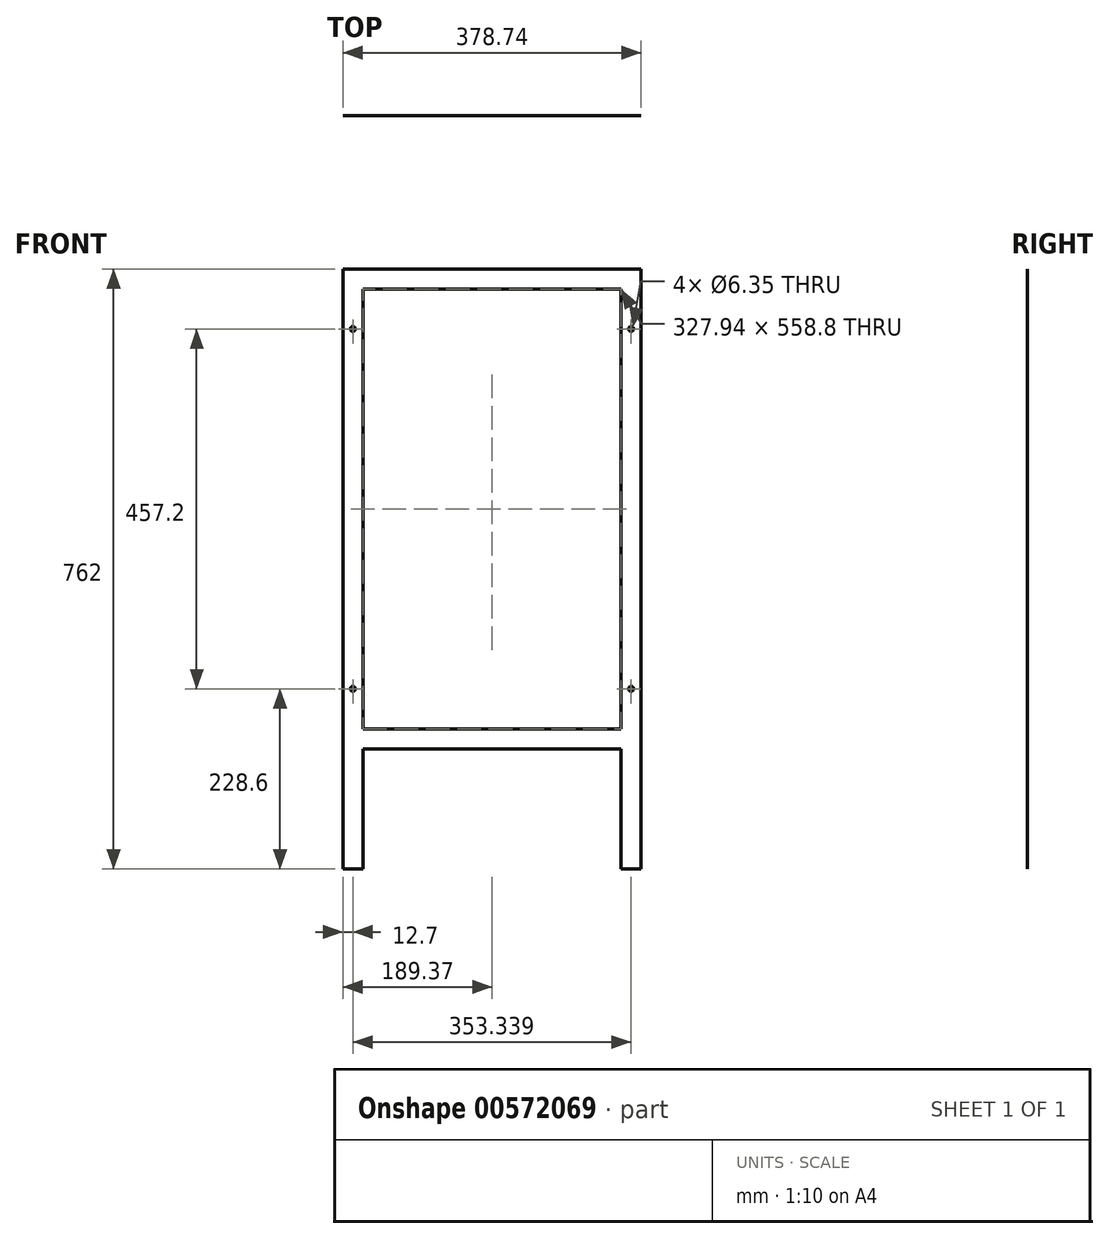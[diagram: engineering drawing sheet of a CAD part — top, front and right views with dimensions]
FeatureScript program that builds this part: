
annotation { "Feature Type Name" : "Feature", "Feature Type Description" : "" }
export const myFeature = defineFeature(function(context is Context, id is Id, definition is map)
    precondition{}
    {
        {
            var Q0;
            Q0=qCreatedBy(makeId("Front.planeOp"),FACE);
            var sketch = newSketch(context, id + "F0", { "sketchPlane" : qUnion([Q0])});
            skLineSegment(sketch, "E0.bottom", {"start": v(189.37, -381) * mm, "end": v(-189.37, -381) * mm});
            skLineSegment(sketch, "E0.top", {"start": v(189.37, 381) * mm, "end": v(-189.37, 381) * mm});
            skLineSegment(sketch, "E0.left", {"start": v(189.37, -381) * mm, "end": v(189.37, 381) * mm});
            skLineSegment(sketch, "E0.right", {"start": v(-189.37, -381) * mm, "end": v(-189.37, 381) * mm});
            skPoint(sketch, "E0.middle", {"position": v(0, 0) * mm});
            skLineSegment(sketch, "E1.bottom", {"start": v(-189.37, 381) * mm, "end": v(189.37, 381) * mm});
            skLineSegment(sketch, "E1.top", {"start": v(-189.37, 370.84) * mm, "end": v(189.37, 370.84) * mm});
            skLineSegment(sketch, "E1.left", {"start": v(-189.37, 381) * mm, "end": v(-189.37, 370.84) * mm});
            skLineSegment(sketch, "E1.right", {"start": v(189.37, 381) * mm, "end": v(189.37, 370.84) * mm});
            skSolve(sketch);
        }
        {
            var Q0;
            Q0 = qSketchRegion(id + "F0", true);
            extrude(context, id + "F1", {"entities" : qUnion([Q0]), "depth" : 1 / 254 * mm, "offsetDistance" : 25.4 * mm});
        }
        {
            var Q0;
            Q0=makeQuery(id+"F1.opExtrude","CAP_FACE",FACE,{"disambiguationData":[OSD([sQuery(id+"F0.wireOp",EDGE,"E0.bottom"),sQuery(id+"F0.wireOp",EDGE,"E0.top"),sQuery(id+"F0.wireOp",EDGE,"E0.left"),sQuery(id+"F0.wireOp",EDGE,"E0.right")])],"isStart":false});
            var sketch = newSketch(context, id + "F2", { "sketchPlane" : qUnion([Q0])});
            skLineSegment(sketch, "E2.bottom", {"start": v(-163.97, -228.6) * mm, "end": v(163.97, -228.6) * mm});
            skLineSegment(sketch, "E2.top", {"start": v(-163.97, -381) * mm, "end": v(163.97, -381) * mm});
            skLineSegment(sketch, "E2.left", {"start": v(-163.97, -228.6) * mm, "end": v(-163.97, -381) * mm});
            skLineSegment(sketch, "E2.right", {"start": v(163.97, -228.6) * mm, "end": v(163.97, -381) * mm});
            skLineSegment(sketch, "E3.bottom", {"start": v(-163.97, 355.6) * mm, "end": v(163.97, 355.6) * mm});
            skLineSegment(sketch, "E3.top", {"start": v(-163.97, -203.2) * mm, "end": v(163.97, -203.2) * mm});
            skLineSegment(sketch, "E3.left", {"start": v(-163.97, 355.6) * mm, "end": v(-163.97, -203.2) * mm});
            skLineSegment(sketch, "E3.right", {"start": v(163.97, 355.6) * mm, "end": v(163.97, -203.2) * mm});
            skCircle(sketch, "E4", {"center": v(176.67, 304.8) * mm, "radius": 3.17 * mm});
            skCircle(sketch, "E5", {"center": v(176.67, -152.4) * mm, "radius": 3.17 * mm});
            skCircle(sketch, "E6", {"center": v(-176.67, -152.4) * mm, "radius": 3.17 * mm});
            skCircle(sketch, "E7", {"center": v(-176.67, 304.8) * mm, "radius": 3.18 * mm});
            skLineSegment(sketch, "E8", {"start": v(176.67, 304.8) * mm, "end": v(178.13, 307.62) * mm});
            skLineSegment(sketch, "E9", {"start": v(-176.67, 304.8) * mm, "end": v(-173.5, 304.8) * mm});
            skLineSegment(sketch, "E10", {"start": v(176.67, -152.4) * mm, "end": v(176.67, -149.23) * mm});
            skLineSegment(sketch, "E11", {"start": v(-176.67, -152.4) * mm, "end": v(-176.67, -149.23) * mm});
            skSolve(sketch);
        }
        {
            var Q0;
            Q0 = qSketchRegion(id + "F2", true);
            extrude(context, id + "F3", {"entities" : qUnion([Q0]), "operationType" : NewBodyOperationType.REMOVE, "endBound" : BoundingType.THROUGH_ALL, "oppositeDirection" : true, "depth" : 25.4 * mm, "offsetDistance" : 25.4 * mm});
        }
    });
